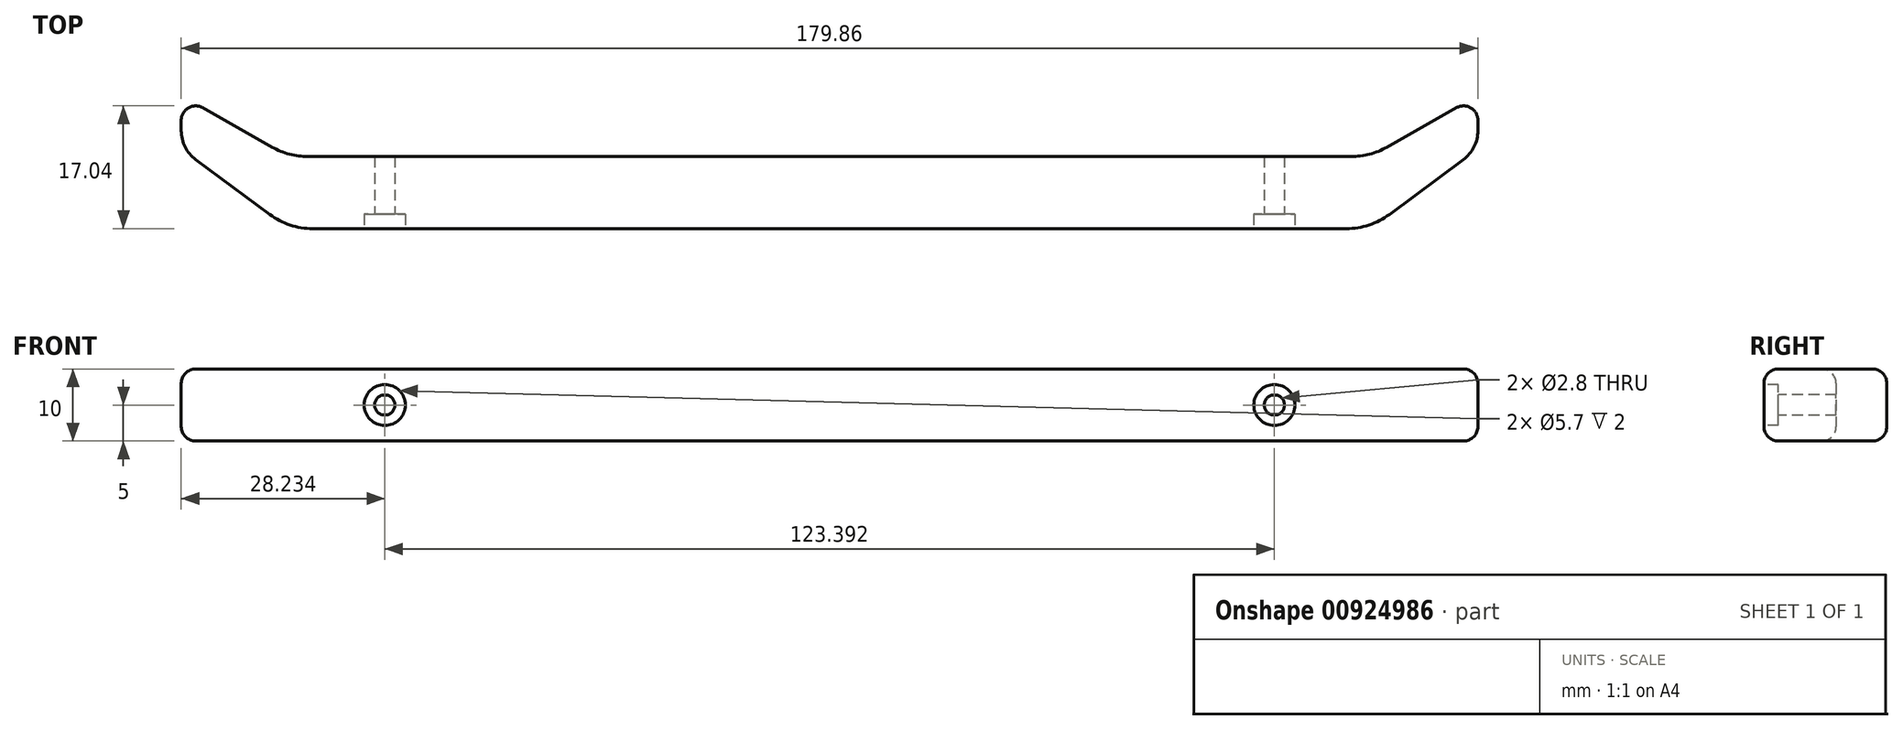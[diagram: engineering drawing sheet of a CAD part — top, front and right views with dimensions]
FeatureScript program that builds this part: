
annotation { "Feature Type Name" : "Feature", "Feature Type Description" : "" }
export const myFeature = defineFeature(function(context is Context, id is Id, definition is map)
    precondition{}
    {
        {
            var Q0;
            Q0=qCreatedBy(makeId("Top.planeOp"),FACE);
            var sketch = newSketch(context, id + "F0", { "sketchPlane" : qUnion([Q0])});
            skLineSegment(sketch, "E0.bottom", {"start": v(72.36, 5) * mm, "end": v(0, 5) * mm});
            skLineSegment(sketch, "E0.top", {"start": v(71.7, -5) * mm, "end": v(0, -5) * mm});
            skPoint(sketch, "E0.middle", {"position": v(0, 0) * mm});
            skLineSegment(sketch, "E1", {"start": v(0, 68.72) * mm, "end": v(0, -60.5) * mm, "construction": true});
            skPoint(sketch, "E2.MirrorP", {"position": v(75, 5) * mm});
            skArc(sketch, "E3.MirrorCS", {"start": v(77.3, 6.3) * mm, "mid": v(74.91, 5.33) * mm, "end": v(72.36, 5) * mm});
            skLineSegment(sketch, "E4.MirrorCS", {"start": v(77.3, 6.3) * mm, "end": v(86.94, 11.78) * mm});
            skLineSegment(sketch, "E5.MirrorCS", {"start": v(77.65, -3.03) * mm, "end": v(87.91, 4.58) * mm});
            skArc(sketch, "E6.MirrorCS", {"start": v(77.65, -3.03) * mm, "mid": v(74.83, -4.5) * mm, "end": v(71.7, -5) * mm});
            skArc(sketch, "E7.MirrorCS", {"start": v(89.93, 8.6) * mm, "mid": v(89.4, 6.35) * mm, "end": v(87.91, 4.58) * mm});
            skArc(sketch, "E8.MirrorCS", {"start": v(86.94, 11.78) * mm, "mid": v(88.94, 11.77) * mm, "end": v(89.93, 10.04) * mm});
            skLineSegment(sketch, "E9.MirrorCS", {"start": v(89.93, 10.04) * mm, "end": v(89.93, 8.6) * mm});
            skPoint(sketch, "E0.left.end.orphan", {"position": v(75, -5) * mm});
            skLineSegment(sketch, "E10", {"start": v(0, -5) * mm, "end": v(0, 5) * mm});
            skSolve(sketch);
        }
        {
            var Q0;
            Q0 = qSketchRegion(id + "F0", true);
            extrude(context, id + "F1", {"entities" : qUnion([Q0]), "depth" : 10 * mm, "offsetDistance" : 25 * mm});
        }
        {
            var Q0;
            Q0=makeQuery(id+"F1.opExtrude","CAP_EDGE",EDGE,{"disambiguationData":[OSD([sQuery(id+"F0.wireOp",EDGE,"E0.top")])],"isStart":false});
            var Q1;
            Q1=makeQuery(id+"F1.opExtrude","CAP_EDGE",EDGE,{"disambiguationData":[OSD([sQuery(id+"F0.wireOp",EDGE,"E0.top")])],"isStart":true});
            fillet(context, id + "F2", {"entities" : qUnion([Q0, Q1]), "radius" : 2 * mm, "tangentPropagation" : true, "allowEdgeOverflow" : false});
        }
        {
            var Q0;
            Q0=makeQuery(id+"F1.opExtrude","SWEPT_FACE",FACE,{"disambiguationData":[OSD([sQuery(id+"F0.wireOp",EDGE,"E0.top")])]});
            var sketch = newSketch(context, id + "F3", { "sketchPlane" : qUnion([Q0])});
            skLineSegment(sketch, "E11", {"start": v(71.7, 5) * mm, "end": v(71.7, 5) * mm});
            skLineSegment(sketch, "E12", {"start": v(61.7, 2) * mm, "end": v(61.7, 8) * mm, "construction": true});
            skCircle(sketch, "E13", {"center": v(61.7, 5) * mm, "radius": 1.4 * mm});
            skCircle(sketch, "E14", {"center": v(61.7, 5) * mm, "radius": 2.85 * mm});
            skSolve(sketch);
        }
        {
            var Q0;
            Q0=makeQuery(id+"F3.imprint","IMPRINT",FACE,{"disambiguationData":[TD([[makeQuery(id+"F3.imprint","IMPRINT",EDGE,{"derivedFrom":sQuery(id+"F3.wireOp",EDGE,"E13")}),1.0]])]});
            extrude(context, id + "F4", {"entities" : qUnion([Q0]), "operationType" : NewBodyOperationType.REMOVE, "oppositeDirection" : true, "depth" : 11 * mm, "offsetDistance" : 25 * mm});
        }
        {
            var Q0;
            Q0 = qSketchRegion(id + "F3", true);
            extrude(context, id + "F5", {"entities" : qUnion([Q0]), "operationType" : NewBodyOperationType.REMOVE, "oppositeDirection" : true, "depth" : 2 * mm, "offsetDistance" : 25 * mm});
        }
        {
            var Q0;
            Q0=makeQuery(id+"F1.opExtrude","SWEPT_BODY",BODY,{"disambiguationData":[OSD([sQuery(id+"F0.wireOp",EDGE,"E0.bottom"),sQuery(id+"F0.wireOp",EDGE,"E0.top"),sQuery(id+"F0.wireOp",EDGE,"E3.MirrorCS"),sQuery(id+"F0.wireOp",EDGE,"E5.MirrorCS"),sQuery(id+"F0.wireOp",EDGE,"E6.MirrorCS"),sQuery(id+"F0.wireOp",EDGE,"E7.MirrorCS"),sQuery(id+"F0.wireOp",EDGE,"E8.MirrorCS"),sQuery(id+"F0.wireOp",EDGE,"E4.MirrorCS"),sQuery(id+"F0.wireOp",EDGE,"E9.MirrorCS"),sQuery(id+"F0.wireOp",EDGE,"E10")])]});
            var Q1;
            Q1=qCreatedBy(makeId("Right.planeOp"),FACE);
            mirror(context, id + "F6", {"operationType" : NewBodyOperationType.ADD, "entities" : qUnion([Q0]), "mirrorPlane" : qUnion([Q1])});
        }
    });
